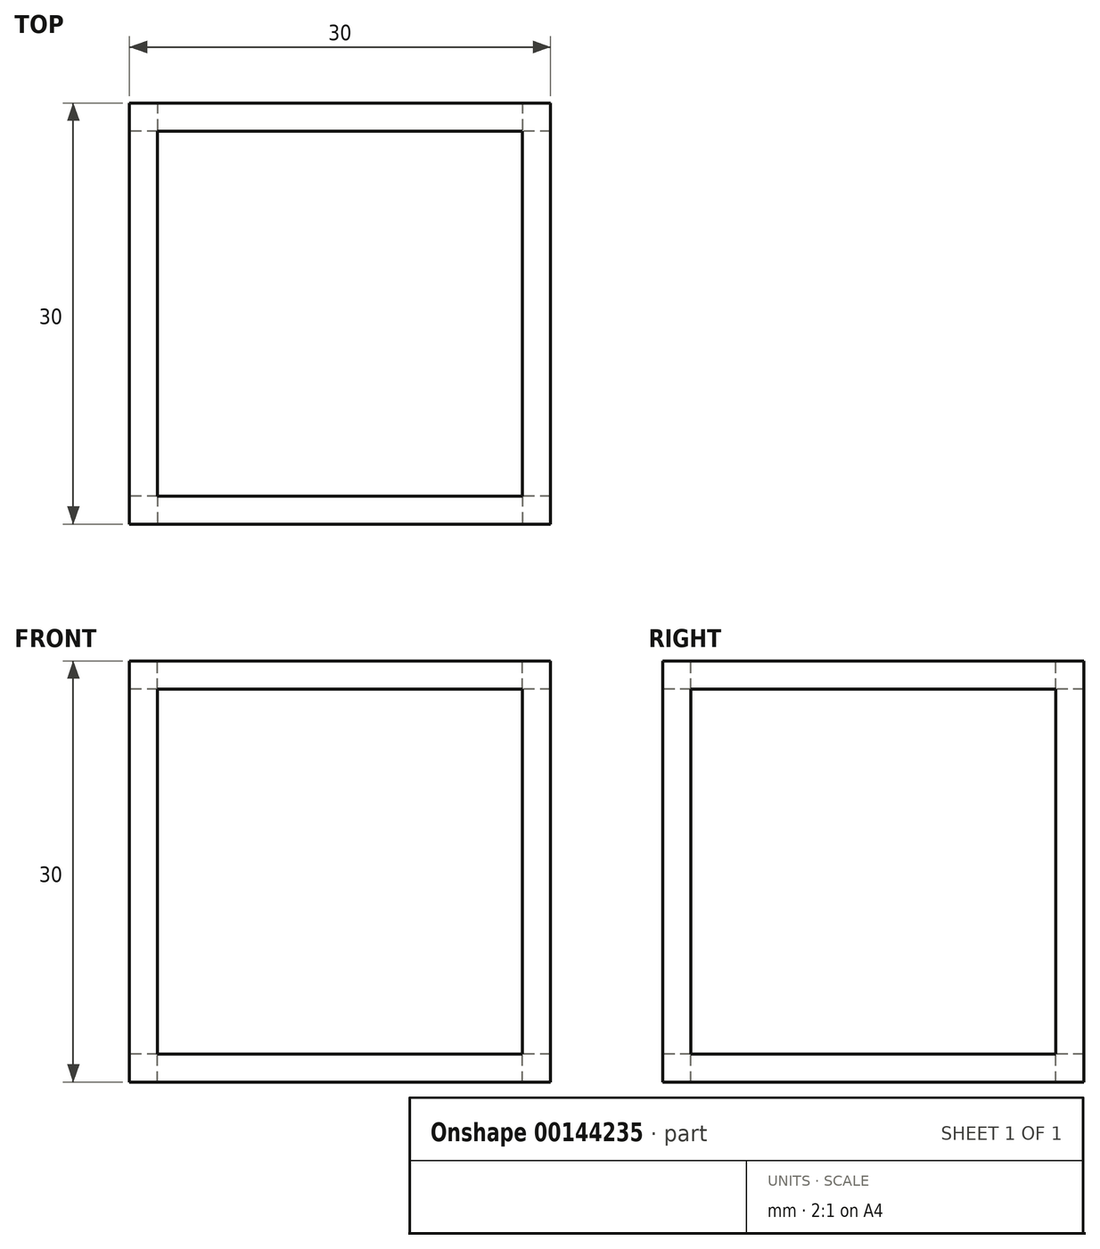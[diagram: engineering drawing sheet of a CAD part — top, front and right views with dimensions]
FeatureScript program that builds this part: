
annotation { "Feature Type Name" : "Feature", "Feature Type Description" : "" }
export const myFeature = defineFeature(function(context is Context, id is Id, definition is map)
    precondition{}
    {
        {
            var Q0;
            Q0=qCreatedBy(makeId("Right.planeOp"),FACE);
            var sketch = newSketch(context, id + "F0", { "sketchPlane" : qUnion([Q0])});
            skLineSegment(sketch, "E0.bottom", {"start": v(0, 0) * mm, "end": v(30, 0) * mm});
            skLineSegment(sketch, "E0.top", {"start": v(0, 30) * mm, "end": v(30, 30) * mm});
            skLineSegment(sketch, "E0.left", {"start": v(0, 0) * mm, "end": v(0, 30) * mm});
            skLineSegment(sketch, "E0.right", {"start": v(30, 0) * mm, "end": v(30, 30) * mm});
            skSolve(sketch);
        }
        {
            var Q0;
            Q0=makeQuery(id+"F0.imprint","IMPRINT",FACE,{"disambiguationData":[TD([[makeQuery(id+"F0.imprint","IMPRINT",EDGE,{"derivedFrom":sQuery(id+"F0.wireOp",EDGE,"E0.bottom")}),1.0]])]});
            extrude(context, id + "F1", {"entities" : qUnion([Q0]), "depth" : 30 * mm});
        }
        {
            var Q0;
            Q0=makeQuery(id+"F1.opExtrude","SWEPT_FACE",FACE,{"disambiguationData":[OSD([sQuery(id+"F0.wireOp",EDGE,"E0.left")])]});
            var sketch = newSketch(context, id + "F2", { "sketchPlane" : qUnion([Q0])});
            skLineSegment(sketch, "E1.bottom", {"start": v(2, 2) * mm, "end": v(28, 2) * mm});
            skLineSegment(sketch, "E1.top", {"start": v(2, 28) * mm, "end": v(28, 28) * mm});
            skLineSegment(sketch, "E1.left", {"start": v(2, 2) * mm, "end": v(2, 28) * mm});
            skLineSegment(sketch, "E1.right", {"start": v(28, 2) * mm, "end": v(28, 28) * mm});
            skSolve(sketch);
        }
        {
            var Q0;
            Q0=makeQuery(id+"F2.imprint","IMPRINT",FACE,{"disambiguationData":[TD([[makeQuery(id+"F2.imprint","IMPRINT",EDGE,{"derivedFrom":sQuery(id+"F2.wireOp",EDGE,"E1.bottom")}),1.0]])]});
            extrude(context, id + "F3", {"entities" : qUnion([Q0]), "operationType" : NewBodyOperationType.REMOVE, "endBound" : BoundingType.THROUGH_ALL, "oppositeDirection" : true, "depth" : 25 * mm});
        }
        {
            var Q0;
            Q0=makeQuery(id+"F1.opExtrude","CAP_FACE",FACE,{"disambiguationData":[OSD([sQuery(id+"F0.wireOp",EDGE,"E0.bottom"),sQuery(id+"F0.wireOp",EDGE,"E0.top"),sQuery(id+"F0.wireOp",EDGE,"E0.left"),sQuery(id+"F0.wireOp",EDGE,"E0.right")])],"isStart":true});
            var sketch = newSketch(context, id + "F4", { "sketchPlane" : qUnion([Q0])});
            skLineSegment(sketch, "E2.bottom", {"start": v(-2, 2) * mm, "end": v(-28, 2) * mm});
            skLineSegment(sketch, "E2.top", {"start": v(-2, 28) * mm, "end": v(-28, 28) * mm});
            skLineSegment(sketch, "E2.left", {"start": v(-2, 2) * mm, "end": v(-2, 28) * mm});
            skLineSegment(sketch, "E2.right", {"start": v(-28, 2) * mm, "end": v(-28, 28) * mm});
            skSolve(sketch);
        }
        {
            var Q0;
            Q0=makeQuery(id+"F4.imprint","IMPRINT",FACE,{"disambiguationData":[TD([[makeQuery(id+"F4.imprint","IMPRINT",EDGE,{"derivedFrom":sQuery(id+"F4.wireOp",EDGE,"E2.bottom")}),-1.0]])]});
            extrude(context, id + "F5", {"entities" : qUnion([Q0]), "operationType" : NewBodyOperationType.REMOVE, "endBound" : BoundingType.THROUGH_ALL, "oppositeDirection" : true, "depth" : 25 * mm});
        }
        {
            var Q0;
            Q0=makeQuery(id+"F1.opExtrude","SWEPT_FACE",FACE,{"disambiguationData":[OSD([sQuery(id+"F0.wireOp",EDGE,"E0.top")])]});
            var sketch = newSketch(context, id + "F6", { "sketchPlane" : qUnion([Q0])});
            skLineSegment(sketch, "E3.bottom", {"start": v(2, 2) * mm, "end": v(28, 2) * mm});
            skLineSegment(sketch, "E3.top", {"start": v(2, 28) * mm, "end": v(28, 28) * mm});
            skLineSegment(sketch, "E3.left", {"start": v(2, 2) * mm, "end": v(2, 28) * mm});
            skLineSegment(sketch, "E3.right", {"start": v(28, 2) * mm, "end": v(28, 28) * mm});
            skSolve(sketch);
        }
        {
            var Q0;
            Q0=makeQuery(id+"F6.imprint","IMPRINT",FACE,{"disambiguationData":[TD([[makeQuery(id+"F6.imprint","IMPRINT",EDGE,{"derivedFrom":sQuery(id+"F6.wireOp",EDGE,"E3.bottom")}),1.0]])]});
            extrude(context, id + "F7", {"entities" : qUnion([Q0]), "operationType" : NewBodyOperationType.REMOVE, "endBound" : BoundingType.THROUGH_ALL, "oppositeDirection" : true, "depth" : 25 * mm});
        }
    });
